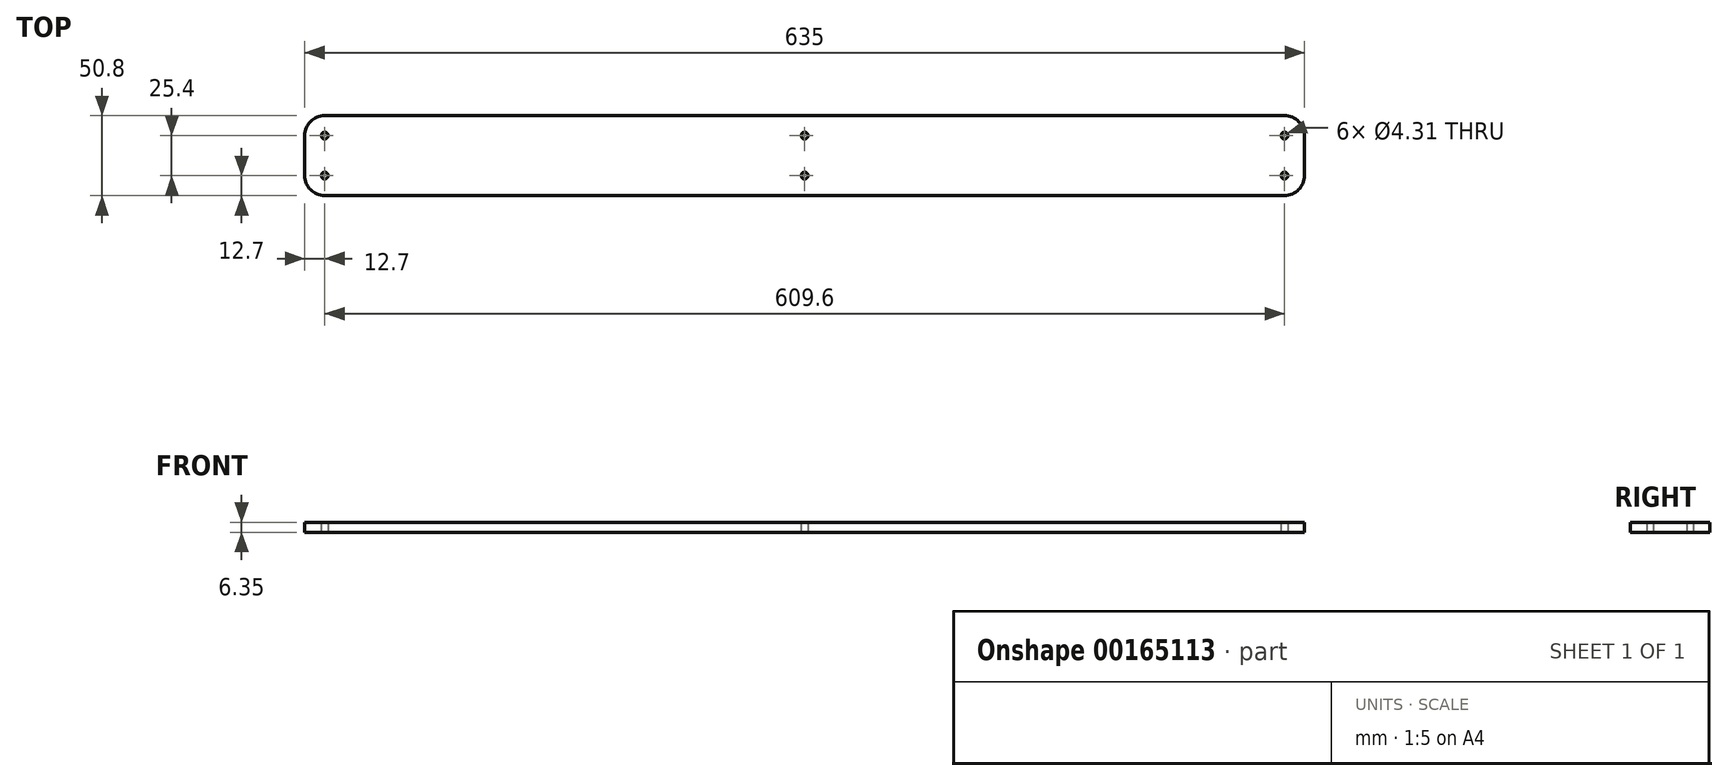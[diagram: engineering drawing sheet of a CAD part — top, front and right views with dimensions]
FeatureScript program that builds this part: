
annotation { "Feature Type Name" : "Feature", "Feature Type Description" : "" }
export const myFeature = defineFeature(function(context is Context, id is Id, definition is map)
    precondition{}
    {
        {
            var Q0;
            Q0=qCreatedBy(makeId("Top.planeOp"),FACE);
            var sketch = newSketch(context, id + "F0", { "sketchPlane" : qUnion([Q0])});
            skLineSegment(sketch, "E0.bottom", {"start": v(-304.8, -12.7) * mm, "end": v(304.8, -12.7) * mm, "construction": true});
            skLineSegment(sketch, "E0.top", {"start": v(-304.8, 12.7) * mm, "end": v(304.8, 12.7) * mm, "construction": true});
            skLineSegment(sketch, "E0.left", {"start": v(-304.8, -12.7) * mm, "end": v(-304.8, 12.7) * mm, "construction": true});
            skLineSegment(sketch, "E0.right", {"start": v(304.8, -12.7) * mm, "end": v(304.8, 12.7) * mm, "construction": true});
            skPoint(sketch, "E0.middle", {"position": v(0, 0) * mm});
            skLineSegment(sketch, "E1.bottom", {"start": v(-317.5, -25.4) * mm, "end": v(317.5, -25.4) * mm});
            skLineSegment(sketch, "E1.top", {"start": v(-317.5, 25.4) * mm, "end": v(317.5, 25.4) * mm});
            skLineSegment(sketch, "E1.left", {"start": v(-317.5, -25.4) * mm, "end": v(-317.5, 25.4) * mm});
            skLineSegment(sketch, "E1.right", {"start": v(317.5, -25.4) * mm, "end": v(317.5, 25.4) * mm});
            skLineSegment(sketch, "E2", {"start": v(304.8, -12.7) * mm, "end": v(317.5, -12.7) * mm, "construction": true});
            skLineSegment(sketch, "E3", {"start": v(304.8, -12.7) * mm, "end": v(304.8, -25.4) * mm, "construction": true});
            skCircle(sketch, "E4", {"center": v(304.8, -12.7) * mm, "radius": 2.15 * mm});
            skCircle(sketch, "E5", {"center": v(304.8, 12.7) * mm, "radius": 2.15 * mm});
            skCircle(sketch, "E6", {"center": v(-304.8, 12.7) * mm, "radius": 2.15 * mm});
            skCircle(sketch, "E7", {"center": v(-304.8, -12.7) * mm, "radius": 2.15 * mm});
            skCircle(sketch, "E8", {"center": v(0, 12.7) * mm, "radius": 2.15 * mm});
            skCircle(sketch, "E9", {"center": v(0, -12.7) * mm, "radius": 2.15 * mm});
            skSolve(sketch);
        }
        {
            var Q0;
            Q0 = qSketchRegion(id + "F0", true);
            extrude(context, id + "F1", {"entities" : qUnion([Q0]), "depth" : 6.35 * mm});
        }
        {
            var Q0;
            Q0=makeQuery(id+"F1.opExtrude","SWEPT_EDGE",EDGE,{"disambiguationData":[OSD([sQuery(id+"F0.wireOp",EDGE,"E1.top"),sQuery(id+"F0.wireOp",EDGE,"E1.right")])]});
            var Q1;
            Q1=makeQuery(id+"F1.opExtrude","SWEPT_EDGE",EDGE,{"disambiguationData":[OSD([sQuery(id+"F0.wireOp",EDGE,"E1.bottom"),sQuery(id+"F0.wireOp",EDGE,"E1.right")])]});
            var Q2;
            Q2=makeQuery(id+"F1.opExtrude","SWEPT_EDGE",EDGE,{"disambiguationData":[OSD([sQuery(id+"F0.wireOp",EDGE,"E1.bottom"),sQuery(id+"F0.wireOp",EDGE,"E1.left")])]});
            var Q3;
            Q3=makeQuery(id+"F1.opExtrude","SWEPT_EDGE",EDGE,{"disambiguationData":[OSD([sQuery(id+"F0.wireOp",EDGE,"E1.top"),sQuery(id+"F0.wireOp",EDGE,"E1.left")])]});
            fillet(context, id + "F2", {"entities" : qUnion([Q0, Q1, Q2, Q3]), "radius" : 12.7 * mm, "tangentPropagation" : true, "allowEdgeOverflow" : false});
        }
    });
